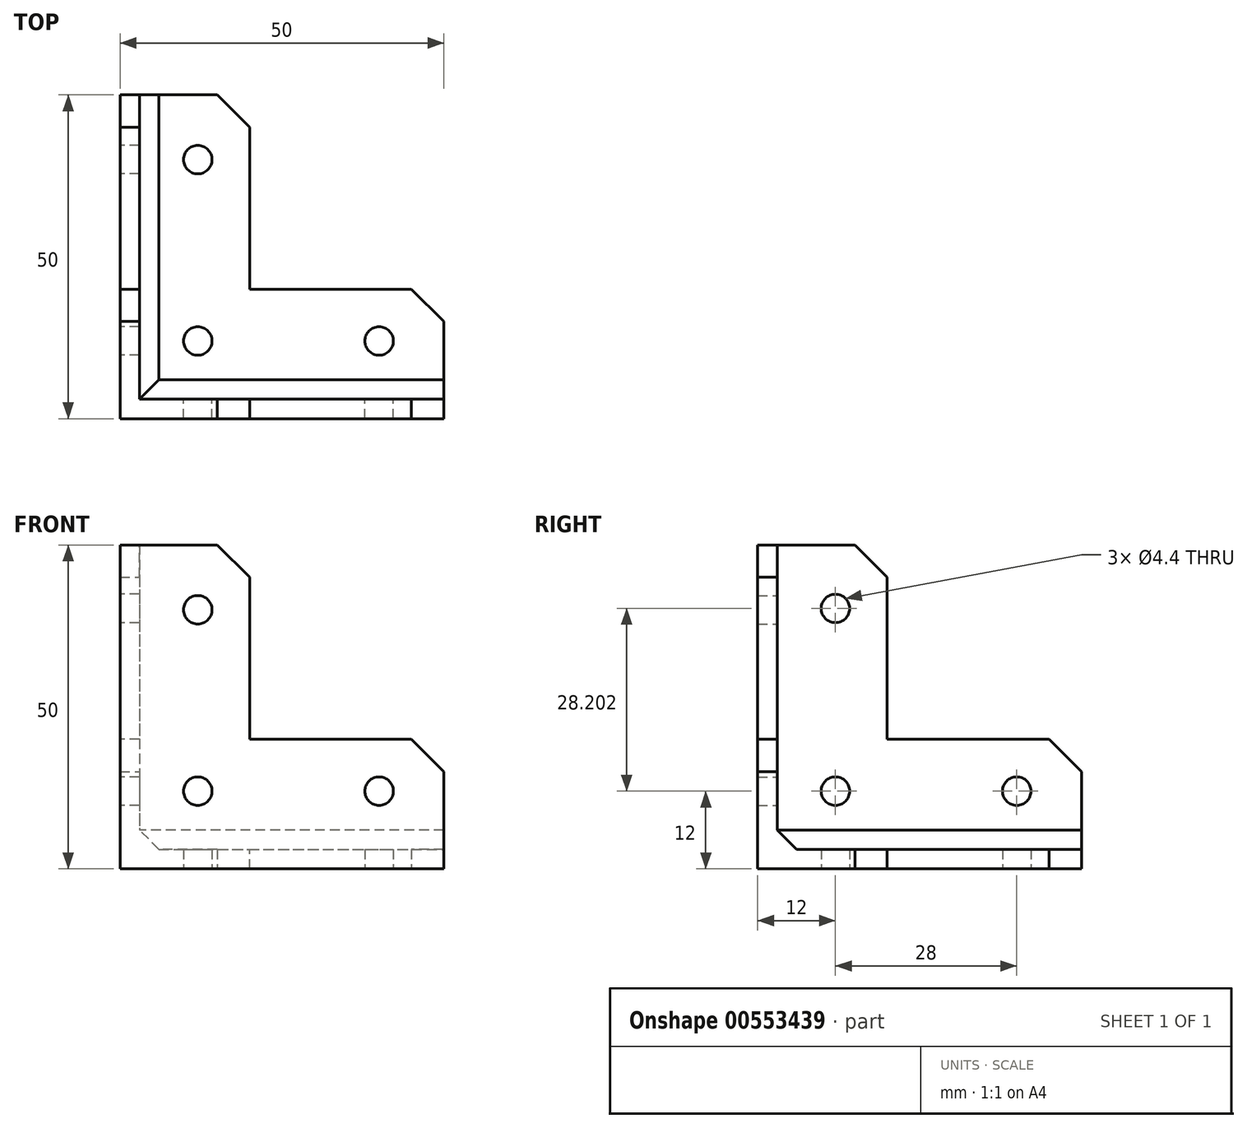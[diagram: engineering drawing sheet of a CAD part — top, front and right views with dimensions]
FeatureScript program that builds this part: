
annotation { "Feature Type Name" : "Feature", "Feature Type Description" : "" }
export const myFeature = defineFeature(function(context is Context, id is Id, definition is map)
    precondition{}
    {
        {
            var Q0;
            Q0=qCreatedBy(makeId("Front.planeOp"),FACE);
            var sketch = newSketch(context, id + "F0", { "sketchPlane" : qUnion([Q0])});
            skLineSegment(sketch, "E0", {"start": v(-103.1, 50) * mm, "end": v(-103.1, 0) * mm});
            skLineSegment(sketch, "E1", {"start": v(-103.1, 0) * mm, "end": v(-53.1, 0) * mm});
            skLineSegment(sketch, "E2", {"start": v(-53.1, 0) * mm, "end": v(-53.1, 20) * mm});
            skLineSegment(sketch, "E3", {"start": v(-53.1, 20) * mm, "end": v(-83.1, 20) * mm});
            skLineSegment(sketch, "E4", {"start": v(-83.1, 20) * mm, "end": v(-83.1, 50) * mm});
            skLineSegment(sketch, "E5", {"start": v(-83.1, 50) * mm, "end": v(-103.1, 50) * mm});
            skPoint(sketch, "E6", {"position": v(-91.1, 40) * mm});
            skPoint(sketch, "E6.positionSnap0", {"position": v(-93.1, 50) * mm});
            skPoint(sketch, "E7", {"position": v(-91.1, 12) * mm});
            skPoint(sketch, "E8", {"position": v(-63.1, 12) * mm});
            skPoint(sketch, "E8.positionSnap0", {"position": v(-53.1, 10) * mm});
            skSolve(sketch);
        }
        {
            var Q0;
            Q0=qSketchRegion(id+"F0",true);
            extrude(context, id + "F1", {"entities" : qUnion([Q0]), "depth" : 3 * mm, "offsetDistance" : 25 * mm});
        }
        {
            var Q0;
            Q0=makeQuery(id+"F1.opExtrude","SWEPT_FACE",FACE,{"disambiguationData":[OSD([sQuery(id+"F0.wireOp",EDGE,"E0")])]});
            var sketch = newSketch(context, id + "F2", { "sketchPlane" : qUnion([Q0])});
            skLineSegment(sketch, "E9", {"start": v(3, 50) * mm, "end": v(-17, 50) * mm});
            skLineSegment(sketch, "E10", {"start": v(-17, 50) * mm, "end": v(-17, 20) * mm});
            skLineSegment(sketch, "E11", {"start": v(-17, 20) * mm, "end": v(-47, 20) * mm});
            skLineSegment(sketch, "E12", {"start": v(-47, 20) * mm, "end": v(-47, 0) * mm});
            skLineSegment(sketch, "E13", {"start": v(-47, 0) * mm, "end": v(3, 0) * mm});
            skPoint(sketch, "E14", {"position": v(-9, 40.2) * mm});
            skPoint(sketch, "E14.positionSnap0", {"position": v(-7, 50) * mm});
            skPoint(sketch, "E15", {"position": v(-37, 12) * mm});
            skPoint(sketch, "E15.positionSnap0", {"position": v(-47, 10) * mm});
            skPoint(sketch, "E16", {"position": v(-9, 12) * mm});
            skSolve(sketch);
        }
        {
            var Q0;
            {var subQ1=sQuery(id+"F2.wireOp",EDGE,"E10");Q0=makeQuery(id+"F2.imprint","IMPRINT",FACE,{"disambiguationData":[TD([[makeQuery(id+"F2.imprint","IMPRINT",EDGE,{"derivedFrom":subQ1}),1.0]])]});}
            extrude(context, id + "F3", {"entities" : qUnion([Q0]), "operationType" : NewBodyOperationType.ADD, "oppositeDirection" : true, "depth" : 3 * mm, "offsetDistance" : 25 * mm});
        }
        {
            var Q0;
            Q0=makeQuery(id+"F3.boolean.opBoolean","MERGE",FACE,{"derivedFrom":[makeQuery(id+"F1.opExtrude","SWEPT_FACE",FACE,{"disambiguationData":[OSD([sQuery(id+"F0.wireOp",EDGE,"E1")])]}),makeQuery(id+"F3.opExtrude","SWEPT_FACE",FACE,{"disambiguationData":[OSD([sQuery(id+"F2.wireOp",EDGE,"E13")])]})]});
            var sketch = newSketch(context, id + "F4", { "sketchPlane" : qUnion([Q0])});
            skLineSegment(sketch, "E17", {"start": v(-53.1, 3) * mm, "end": v(-103.1, 3) * mm});
            skLineSegment(sketch, "E18", {"start": v(-103.1, 3) * mm, "end": v(-103.1, -47) * mm});
            skLineSegment(sketch, "E19", {"start": v(-103.1, -47) * mm, "end": v(-83.1, -47) * mm});
            skLineSegment(sketch, "E20", {"start": v(-83.1, -47) * mm, "end": v(-83.1, -17) * mm});
            skLineSegment(sketch, "E21", {"start": v(-83.1, -17) * mm, "end": v(-53.1, -17) * mm});
            skLineSegment(sketch, "E22", {"start": v(-53.1, -17) * mm, "end": v(-53.1, 3) * mm});
            skPoint(sketch, "E23", {"position": v(-63.1, -9) * mm});
            skPoint(sketch, "E23.positionSnap0", {"position": v(-53.1, -7) * mm});
            skPoint(sketch, "E24", {"position": v(-91.1, -37) * mm});
            skPoint(sketch, "E24.positionSnap0", {"position": v(-93.1, -47) * mm});
            skPoint(sketch, "E25", {"position": v(-91.1, -9) * mm});
            skSolve(sketch);
        }
        {
            var Q0;
            Q0=qSketchRegion(id+"F4",true);
            extrude(context, id + "F5", {"entities" : qUnion([Q0]), "operationType" : NewBodyOperationType.ADD, "oppositeDirection" : true, "depth" : 3 * mm, "offsetDistance" : 25 * mm});
        }
        {
            var Q0;
            Q0=sQuery(id+"F0.wireOp",VERTEX,"E8");
            var Q1;
            Q1=sQuery(id+"F0.wireOp",VERTEX,"E6");
            var Q2;
            Q2=sQuery(id+"F0.wireOp",VERTEX,"E7");
            var Q3;
            Q3=makeQuery(id+"F1.opExtrude","SWEPT_BODY",BODY,{"disambiguationData":[OSD([sQuery(id+"F0.wireOp",EDGE,"E0"),sQuery(id+"F0.wireOp",EDGE,"E1"),sQuery(id+"F0.wireOp",EDGE,"E2"),sQuery(id+"F0.wireOp",EDGE,"E3"),sQuery(id+"F0.wireOp",EDGE,"E4"),sQuery(id+"F0.wireOp",EDGE,"E5")])]});
            hole(context, id + "F6", {"style" : HoleStyle.SIMPLE, "endStyle" : HoleEndStyle.BLIND, "oppositeDirection" : true, "standardTappedOrClearance" : lookupTablePath({ "standard" : "ISO", "fit" : "Normal", "size" : "M4", "type" : "Clearance" }), "standardBlindInLast" : lookupTablePath({ "fit" : "Standard", "standard" : "ISO", "size" : "M4", "type" : "Clearance" }), "holeDiameter" : 4.4 * mm, "holeDepth" : 80 * mm, "isTappedThrough" : true, "tappedDepth" : 12 * mm, "tapClearance" : 3, "startFromSketch" : true, "locations" : qUnion([Q0, Q1, Q2]), "scope" : qUnion([Q3])});
        }
        {
            var Q0;
            Q0=sQuery(id+"F2.wireOp",VERTEX,"E14");
            var Q1;
            Q1=sQuery(id+"F4.wireOp",VERTEX,"E25");
            var Q2;
            Q2=sQuery(id+"F2.wireOp",VERTEX,"E15");
            var Q3;
            Q3=sQuery(id+"F2.wireOp",VERTEX,"E16");
            var Q4;
            Q4=sQuery(id+"F4.wireOp",VERTEX,"E24");
            var Q5;
            Q5=sQuery(id+"F4.wireOp",VERTEX,"E23");
            var Q6;
            Q6=makeQuery(id+"F1.opExtrude","SWEPT_BODY",BODY,{"disambiguationData":[OSD([sQuery(id+"F0.wireOp",EDGE,"E0"),sQuery(id+"F0.wireOp",EDGE,"E1"),sQuery(id+"F0.wireOp",EDGE,"E2"),sQuery(id+"F0.wireOp",EDGE,"E3"),sQuery(id+"F0.wireOp",EDGE,"E4"),sQuery(id+"F0.wireOp",EDGE,"E5")])]});
            hole(context, id + "F7", {"style" : HoleStyle.SIMPLE, "endStyle" : HoleEndStyle.BLIND, "standardTappedOrClearance" : lookupTablePath({ "standard" : "ISO", "fit" : "Normal", "size" : "M4", "type" : "Clearance" }), "standardBlindInLast" : lookupTablePath({ "fit" : "Standard", "standard" : "ISO", "size" : "M4", "type" : "Clearance" }), "holeDiameter" : 4.4 * mm, "holeDepth" : 80 * mm, "isTappedThrough" : true, "tappedDepth" : 12 * mm, "tapClearance" : 3, "startFromSketch" : true, "locations" : qUnion([Q0, Q1, Q2, Q3, Q4, Q5]), "scope" : qUnion([Q6])});
        }
        {
            var Q0;
            Q0=makeQuery(id+"F3.opExtrude","CAP_FACE",FACE,{"disambiguationData":[OSD([sQuery(id+"F0.wireOp",EDGE,"E0"),sQuery(id+"F2.wireOp",EDGE,"E9"),sQuery(id+"F2.wireOp",EDGE,"E10"),sQuery(id+"F2.wireOp",EDGE,"E11"),sQuery(id+"F2.wireOp",EDGE,"E12"),sQuery(id+"F2.wireOp",EDGE,"E13")])],"isStart":false});
            var sketch = newSketch(context, id + "F8", { "sketchPlane" : qUnion([Q0])});
            skLineSegment(sketch, "E26.bottom", {"start": v(0, 3) * mm, "end": v(5, 3) * mm});
            skLineSegment(sketch, "E26.top", {"start": v(0, 8) * mm, "end": v(5, 8) * mm});
            skLineSegment(sketch, "E26.left", {"start": v(0, 3) * mm, "end": v(0, 8) * mm});
            skLineSegment(sketch, "E26.right", {"start": v(5, 3) * mm, "end": v(5, 8) * mm});
            skSolve(sketch);
        }
        {
            var Q0;
            Q0=makeQuery(id+"F5.boolean.opBoolean","INTERSECT",EDGE,{"derivedFrom":[makeQuery(id+"F1.opExtrude","CAP_FACE",FACE,{"disambiguationData":[OSD([sQuery(id+"F0.wireOp",EDGE,"E0"),sQuery(id+"F0.wireOp",EDGE,"E1"),sQuery(id+"F0.wireOp",EDGE,"E2"),sQuery(id+"F0.wireOp",EDGE,"E3"),sQuery(id+"F0.wireOp",EDGE,"E4"),sQuery(id+"F0.wireOp",EDGE,"E5")])],"isStart":true}),makeQuery(id+"F5.opExtrude","CAP_FACE",FACE,{"disambiguationData":[OSD([sQuery(id+"F4.wireOp",EDGE,"E17"),sQuery(id+"F4.wireOp",EDGE,"E18"),sQuery(id+"F4.wireOp",EDGE,"E19"),sQuery(id+"F4.wireOp",EDGE,"E20"),sQuery(id+"F4.wireOp",EDGE,"E21"),sQuery(id+"F4.wireOp",EDGE,"E22")])],"isStart":false})]});
            var Q1;
            Q1=makeQuery(id+"F5.boolean.opBoolean","INTERSECT",EDGE,{"derivedFrom":[makeQuery(id+"F3.opExtrude","CAP_FACE",FACE,{"disambiguationData":[OSD([sQuery(id+"F0.wireOp",EDGE,"E0"),sQuery(id+"F2.wireOp",EDGE,"E9"),sQuery(id+"F2.wireOp",EDGE,"E10"),sQuery(id+"F2.wireOp",EDGE,"E11"),sQuery(id+"F2.wireOp",EDGE,"E12"),sQuery(id+"F2.wireOp",EDGE,"E13")])],"isStart":false}),makeQuery(id+"F5.opExtrude","CAP_FACE",FACE,{"disambiguationData":[OSD([sQuery(id+"F4.wireOp",EDGE,"E17"),sQuery(id+"F4.wireOp",EDGE,"E18"),sQuery(id+"F4.wireOp",EDGE,"E19"),sQuery(id+"F4.wireOp",EDGE,"E20"),sQuery(id+"F4.wireOp",EDGE,"E21"),sQuery(id+"F4.wireOp",EDGE,"E22")])],"isStart":false})]});
            var Q2;
            Q2=makeQuery(id+"F3.opExtrude","CAP_EDGE",EDGE,{"disambiguationData":[OSD([sQuery(id+"F0.wireOp",EDGE,"E0")])],"isStart":false});
            chamfer(context, id + "F9", {"entities" : qUnion([Q0, Q1, Q2]), "width" : 3 * mm, "tangentPropagation" : true});
        }
        {
            var Q0;
            Q0=makeQuery(id+"F1.opExtrude","SWEPT_EDGE",EDGE,{"disambiguationData":[OSD([sQuery(id+"F0.wireOp",EDGE,"E2"),sQuery(id+"F0.wireOp",EDGE,"E3")])]});
            var Q1;
            Q1=makeQuery(id+"F5.opExtrude","SWEPT_EDGE",EDGE,{"disambiguationData":[OSD([sQuery(id+"F4.wireOp",EDGE,"E21"),sQuery(id+"F4.wireOp",EDGE,"E22")])]});
            var Q2;
            Q2=makeQuery(id+"F5.opExtrude","SWEPT_EDGE",EDGE,{"disambiguationData":[OSD([sQuery(id+"F4.wireOp",EDGE,"E19"),sQuery(id+"F4.wireOp",EDGE,"E20")])]});
            var Q3;
            Q3=makeQuery(id+"F3.opExtrude","SWEPT_EDGE",EDGE,{"disambiguationData":[OSD([sQuery(id+"F2.wireOp",EDGE,"E11"),sQuery(id+"F2.wireOp",EDGE,"E12")])]});
            var Q4;
            Q4=makeQuery(id+"F1.opExtrude","SWEPT_EDGE",EDGE,{"disambiguationData":[OSD([sQuery(id+"F0.wireOp",EDGE,"E4"),sQuery(id+"F0.wireOp",EDGE,"E5")])]});
            var Q5;
            Q5=makeQuery(id+"F3.opExtrude","SWEPT_EDGE",EDGE,{"disambiguationData":[OSD([sQuery(id+"F2.wireOp",EDGE,"E9"),sQuery(id+"F2.wireOp",EDGE,"E10")])]});
            chamfer(context, id + "F10", {"entities" : qUnion([Q0, Q1, Q2, Q3, Q4, Q5]), "width" : 5 * mm, "tangentPropagation" : true});
        }
    });
